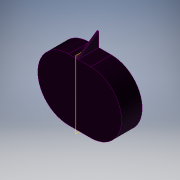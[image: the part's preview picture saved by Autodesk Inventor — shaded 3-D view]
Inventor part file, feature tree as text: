
AUTODESK INVENTOR PART (.ipt)
format: ipt  version: 2019 (Build 230136000, 136)  size: 128,000 bytes
history: native  units: in
note: dims shown in document units (in); Inventor stores cm internally (conversion verified against a paired STEP export)
features: extrude x3, sketch x3, plane x1, mirror x1
ambient origin geometry x8: Origin, YZ Plane, XZ Plane, XY Plane, X Axis, Y Axis, Z Axis, Center Point
bodies: Body1 (feature_tree)
feature tree (8):
  extrude  "Extrusion3"  Depth=156.0in
  extrude  "Extrusion4"  Depth=77.5in
  plane  "Work Plane1"
  extrude  "Extrusion5"  TaperAngle=90.0deg  [1 undecoded]
  mirror  "Mirror1"
  sketch  "Sketch4"  dims[d12=156.0in d13=156.0in]
  sketch  "Sketch6"  dims[d14=0.5in d15=0.0in d18=77.5in]
  sketch  "Sketch8"  dims[d19=77.5in d20=90.0deg d21=52.0in d22=0.0in d23=20.0in d24=36.0in d25=4.0in d26=0.0in]
note: 1 required parameter value undecoded (feature->parameter linkage not recoverable at this tier; creation-order binding heuristic only, values carry confidence <= 0.55)
